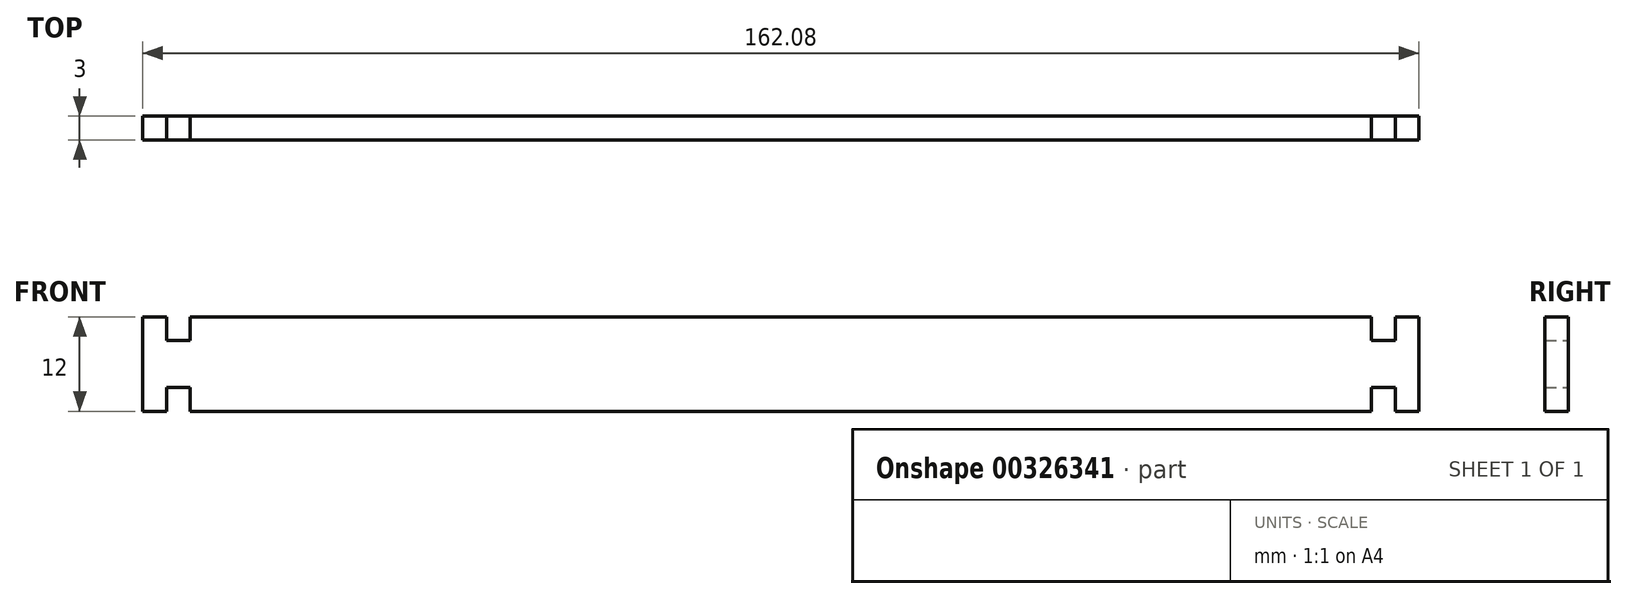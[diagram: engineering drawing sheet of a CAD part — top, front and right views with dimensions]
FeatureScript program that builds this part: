
annotation { "Feature Type Name" : "Feature", "Feature Type Description" : "" }
export const myFeature = defineFeature(function(context is Context, id is Id, definition is map)
    precondition{}
    {
        {
            var Q0;
            Q0=qCreatedBy(makeId("Front.planeOp"),FACE);
            var sketch = newSketch(context, id + "F0", { "sketchPlane" : qUnion([Q0])});
            skPoint(sketch, "E0", {"position": v(-78.04, -2) * mm});
            skPoint(sketch, "E1", {"position": v(-78.04, 1.02) * mm});
            skPoint(sketch, "E2", {"position": v(-75, 1.02) * mm});
            skPoint(sketch, "E3", {"position": v(78.04, -2) * mm});
            skPoint(sketch, "E4", {"position": v(78.04, 1.02) * mm});
            skPoint(sketch, "E5", {"position": v(75, 1.02) * mm});
            skPoint(sketch, "E6", {"position": v(75, -2) * mm});
            skLineSegment(sketch, "E7", {"start": v(-78.04, -2) * mm, "end": v(-78.04, 1.02) * mm});
            skLineSegment(sketch, "E8", {"start": v(-75, 1.02) * mm, "end": v(-78.04, 1.02) * mm});
            skLineSegment(sketch, "E9", {"start": v(-75, -2) * mm, "end": v(-75, 1.02) * mm});
            skLineSegment(sketch, "E10", {"start": v(75, -2) * mm, "end": v(75, 1.02) * mm});
            skLineSegment(sketch, "E11", {"start": v(78.04, 1.02) * mm, "end": v(75, 1.02) * mm});
            skLineSegment(sketch, "E12", {"start": v(78.04, -2) * mm, "end": v(78.04, 1.02) * mm});
            skLineSegment(sketch, "E13.trimOffspring", {"start": v(78.04, -2) * mm, "end": v(81.04, -2) * mm});
            skLineSegment(sketch, "E14.trimOffspring", {"start": v(-78.04, -2) * mm, "end": v(-81.04, -2) * mm});
            skLineSegment(sketch, "E15", {"start": v(-81.04, 10) * mm, "end": v(-78.04, 10) * mm});
            skLineSegment(sketch, "E16", {"start": v(-78.04, 10) * mm, "end": v(-78.04, 6.98) * mm});
            skLineSegment(sketch, "E17", {"start": v(-78.04, 6.98) * mm, "end": v(-75, 6.98) * mm});
            skLineSegment(sketch, "E18", {"start": v(-75, 6.98) * mm, "end": v(-75, 10) * mm});
            skLineSegment(sketch, "E19", {"start": v(81.04, 10) * mm, "end": v(78.04, 10) * mm});
            skLineSegment(sketch, "E20", {"start": v(78.04, 10) * mm, "end": v(78.04, 6.98) * mm});
            skLineSegment(sketch, "E21", {"start": v(78.04, 6.98) * mm, "end": v(75, 6.98) * mm});
            skLineSegment(sketch, "E22", {"start": v(75, 6.98) * mm, "end": v(75, 10) * mm});
            skLineSegment(sketch, "E23", {"start": v(75, 10) * mm, "end": v(-75, 10) * mm});
            skLineSegment(sketch, "E24", {"start": v(81.04, 10) * mm, "end": v(81.04, -2) * mm});
            skLineSegment(sketch, "E25", {"start": v(-81.04, 10) * mm, "end": v(-81.04, -2) * mm});
            skLineSegment(sketch, "E26", {"start": v(-75, -2) * mm, "end": v(75, -2) * mm});
            skSolve(sketch);
        }
        {
            var Q0;
            Q0=makeQuery(id+"F0.imprint","IMPRINT",FACE,{"disambiguationData":[TD([[makeQuery(id+"F0.imprint","IMPRINT",EDGE,{"derivedFrom":sQuery(id+"F0.wireOp",EDGE,"ItmVC9ZI-ysAT-GvL9-55L5-KoOHRsY66XSg")}),-1.0]])]});
            var Q1;
            Q1=makeQuery(id+"F0.imprint","IMPRINT",FACE,{"disambiguationData":[TD([[makeQuery(id+"F0.imprint","IMPRINT",EDGE,{"derivedFrom":sQuery(id+"F0.wireOp",EDGE,"E7")}),1.0]])]});
            extrude(context, id + "F1", {"entities" : qUnion([Q0, Q1]), "depth" : 3 * mm});
        }
    });
